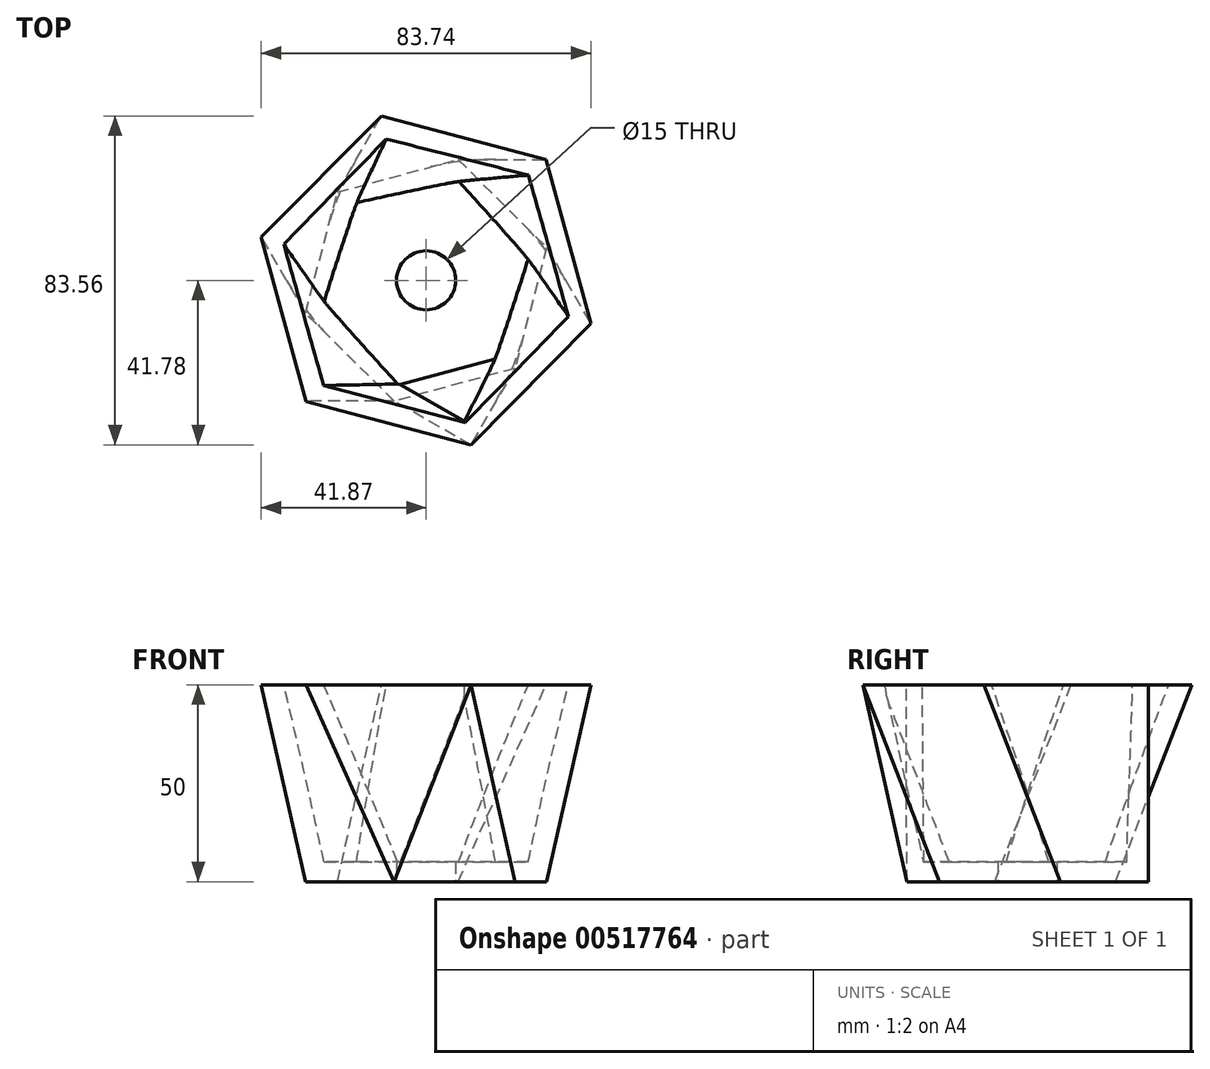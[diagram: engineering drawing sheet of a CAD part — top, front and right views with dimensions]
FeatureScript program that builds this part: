
annotation { "Feature Type Name" : "Feature", "Feature Type Description" : "" }
export const myFeature = defineFeature(function(context is Context, id is Id, definition is map)
    precondition{}
    {
        {
            var Q0;
            Q0=qCreatedBy(makeId("Top.planeOp"),FACE);
            var sketch = newSketch(context, id + "F0", { "sketchPlane" : qUnion([Q0])});
            skCircle(sketch, "E0.cCircle", {"center": v(0, 0) * mm, "radius": 27.5 * mm, "construction": true});
            skLineSegment(sketch, "E0.0", {"start": v(8.1, 30.7) * mm, "end": v(30.64, 8.34) * mm});
            skLineSegment(sketch, "E0.1", {"start": v(30.64, 8.34) * mm, "end": v(22.54, -22.37) * mm});
            skLineSegment(sketch, "E0.2", {"start": v(22.54, -22.37) * mm, "end": v(-8.1, -30.7) * mm});
            skLineSegment(sketch, "E0.3", {"start": v(-8.1, -30.7) * mm, "end": v(-30.64, -8.34) * mm});
            skLineSegment(sketch, "E0.4", {"start": v(-30.64, -8.34) * mm, "end": v(-22.54, 22.37) * mm});
            skLineSegment(sketch, "E0.5", {"start": v(-22.54, 22.37) * mm, "end": v(8.1, 30.7) * mm});
            skPoint(sketch, "E0.0.midPoint", {"position": v(19.37, 19.52) * mm});
            skSolve(sketch);
        }
        {
            var Q0;
            Q0=qCreatedBy(makeId("Top.planeOp"),FACE);
            cPlane(context, id + "F1", {"entities" : qUnion([Q0]), "cplaneType" : CPlaneType.OFFSET, "offset" : 50 * mm, "width" : 150 * mm, "height" : 150 * mm});
        }
        {
            var Q0;
            Q0=qCreatedBy(id+"F1.planeOp",FACE);
            var sketch = newSketch(context, id + "F2", { "sketchPlane" : qUnion([Q0])});
            skCircle(sketch, "E1.cCircle", {"center": v(0, 0) * mm, "radius": 37.5 * mm, "construction": true});
            skLineSegment(sketch, "E1.0", {"start": v(-11.37, 41.78) * mm, "end": v(30.5, 30.74) * mm});
            skLineSegment(sketch, "E1.1", {"start": v(30.5, 30.74) * mm, "end": v(41.87, -11.05) * mm});
            skLineSegment(sketch, "E1.2", {"start": v(41.87, -11.05) * mm, "end": v(11.37, -41.78) * mm});
            skLineSegment(sketch, "E1.3", {"start": v(11.37, -41.78) * mm, "end": v(-30.5, -30.74) * mm});
            skLineSegment(sketch, "E1.4", {"start": v(-30.5, -30.74) * mm, "end": v(-41.87, 11.05) * mm});
            skLineSegment(sketch, "E1.5", {"start": v(-41.87, 11.05) * mm, "end": v(-11.37, 41.78) * mm});
            skPoint(sketch, "E1.0.midPoint", {"position": v(9.57, 36.26) * mm});
            skLineSegment(sketch, "E2", {"start": v(-36.18, -9.85) * mm, "end": v(36.18, 9.85) * mm, "construction": true});
            skPoint(sketch, "E3.0", {"position": v(-30.64, -8.34) * mm});
            skSolve(sketch);
        }
        {
            var Q0;
            Q0=sQuery(id+"F2.wireOp",VERTEX,"E1.4.start");
            var Q1;
            Q1=sQuery(id+"F2.wireOp",VERTEX,"E1.3.start");
            var Q2;
            Q2=sQuery(id+"F0.wireOp",VERTEX,"E0.3.start");
            cPlane(context, id + "F3", {"entities" : qUnion([Q0, Q1, Q2]), "cplaneType" : CPlaneType.THREE_POINT, "offset" : 25 * mm, "width" : 150 * mm, "height" : 150 * mm});
        }
        {
            var Q0;
            Q0=qCreatedBy(id+"F3.planeOp",FACE);
            var sketch = newSketch(context, id + "F4", { "sketchPlane" : qUnion([Q0])});
            skPoint(sketch, "E4.0", {"position": v(-23.27, 53.28) * mm});
            skPoint(sketch, "E5.0", {"position": v(-0.1, 3.62) * mm});
            skPoint(sketch, "E6.0", {"position": v(20.02, 54.58) * mm});
            skLineSegment(sketch, "E7", {"start": v(-23.27, 53.28) * mm, "end": v(-0.1, 3.62) * mm});
            skLineSegment(sketch, "E8", {"start": v(-23.27, 53.28) * mm, "end": v(20.02, 54.58) * mm});
            skLineSegment(sketch, "E9", {"start": v(20.02, 54.58) * mm, "end": v(-0.1, 3.62) * mm});
            skSolve(sketch);
        }
        {
            var Q0;
            Q0=sQuery(id+"F4.wireOp",VERTEX,"E6.0");
            var Q1;
            Q1=sQuery(id+"F4.wireOp",VERTEX,"E5.0");
            var Q2;
            Q2=sQuery(id+"F0.wireOp",VERTEX,"E0.2.start");
            cPlane(context, id + "F5", {"entities" : qUnion([Q0, Q1, Q2]), "cplaneType" : CPlaneType.THREE_POINT, "offset" : 25 * mm, "width" : 150 * mm, "height" : 150 * mm});
        }
        {
            var Q0;
            Q0=qCreatedBy(id+"F5.planeOp",FACE);
            var sketch = newSketch(context, id + "F6", { "sketchPlane" : qUnion([Q0])});
            skPoint(sketch, "E10.0", {"position": v(-4.96, 60.52) * mm});
            skPoint(sketch, "E11.0", {"position": v(15.15, 9.56) * mm});
            skPoint(sketch, "E12.0", {"position": v(-16.5, 6.96) * mm});
            skLineSegment(sketch, "E13", {"start": v(-4.96, 60.52) * mm, "end": v(15.15, 9.56) * mm});
            skLineSegment(sketch, "E14", {"start": v(-16.5, 6.96) * mm, "end": v(-4.96, 60.52) * mm});
            skLineSegment(sketch, "E15", {"start": v(15.15, 9.56) * mm, "end": v(-16.5, 6.96) * mm});
            skSolve(sketch);
        }
        {
            var Q0;
            Q0=makeQuery(id+"F0.imprint","IMPRINT",FACE,{"disambiguationData":[TD([[makeQuery(id+"F0.imprint","IMPRINT",EDGE,{"derivedFrom":sQuery(id+"F0.wireOp",EDGE,"E0.0")}),-1.0]])]});
            var Q1;
            Q1=makeQuery(id+"F2.imprint","IMPRINT",FACE,{"disambiguationData":[TD([[makeQuery(id+"F2.imprint","IMPRINT",EDGE,{"derivedFrom":sQuery(id+"F2.wireOp",EDGE,"E1.0")}),-1.0]])]});
            loft(context, id + "F7", {"sheetProfilesArray" : [{ "sheetProfileEntities" : qUnion([Q0]) }, { "sheetProfileEntities" : qUnion([Q1]) }]});
        }
        {
            var Q0;
            Q0 = qSketchRegion(id + "F6", true);
            var Q1;
            Q1 = qSketchRegion(id + "F4", true);
            var Q2;
            Q2=makeQuery(id+"F7.opLoft","SWEPT_BODY",BODY,{"disambiguationData":[OSD([makeQuery(id+"F0.imprint","IMPRINT",FACE,{"disambiguationData":[TD([[makeQuery(id+"F0.imprint","IMPRINT",EDGE,{"derivedFrom":sQuery(id+"F0.wireOp",EDGE,"E0.0")}),-1.0]])]}),makeQuery(id+"F2.imprint","IMPRINT",FACE,{"disambiguationData":[TD([[makeQuery(id+"F2.imprint","IMPRINT",EDGE,{"derivedFrom":sQuery(id+"F2.wireOp",EDGE,"E1.0")}),-1.0]])]})])]});
            extrude(context, id + "F8", {"entities" : qUnion([Q0, Q1]), "operationType" : NewBodyOperationType.ADD, "endBound" : BoundingType.UP_TO_BODY, "depth" : 25 * mm, "endBoundEntityBody" : qUnion([Q2]), "offsetDistance" : 25 * mm});
        }
        {
            var Q0;
            Q0=makeQuery(id+"F7.opLoft","CAP_FACE",FACE,{"disambiguationData":[OSD([makeQuery(id+"F2.imprint","IMPRINT",FACE,{"disambiguationData":[TD([[makeQuery(id+"F2.imprint","IMPRINT",EDGE,{"derivedFrom":sQuery(id+"F2.wireOp",EDGE,"E1.0")}),-1.0]])]})])],"isStart":true});
            shell(context, id + "F9", {"entities" : qUnion([Q0]), "thickness" : 5 * mm});
        }
        {
            var Q0;
            Q0=sQuery(id+"F0.wireOp",VERTEX,"E0.cCircle.center");
            var Q1;
            Q1=makeQuery(id+"F7.opLoft","SWEPT_BODY",BODY,{"disambiguationData":[OSD([makeQuery(id+"F0.imprint","IMPRINT",FACE,{"disambiguationData":[TD([[makeQuery(id+"F0.imprint","IMPRINT",EDGE,{"derivedFrom":sQuery(id+"F0.wireOp",EDGE,"E0.0")}),-1.0]])]}),makeQuery(id+"F2.imprint","IMPRINT",FACE,{"disambiguationData":[TD([[makeQuery(id+"F2.imprint","IMPRINT",EDGE,{"derivedFrom":sQuery(id+"F2.wireOp",EDGE,"E1.0")}),-1.0]])]})])]});
            hole(context, id + "F10", {"style" : HoleStyle.SIMPLE, "endStyle" : HoleEndStyle.THROUGH, "oppositeDirection" : true, "holeDiameter" : 15 * mm, "isTappedThrough" : true, "tappedDepth" : 12 * mm, "tapClearance" : 3, "startFromSketch" : true, "locations" : qUnion([Q0]), "scope" : qUnion([Q1])});
        }
    });
